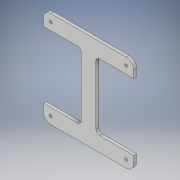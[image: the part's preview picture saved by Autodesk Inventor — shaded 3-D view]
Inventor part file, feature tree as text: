
AUTODESK INVENTOR PART (.ipt)
format: ipt  version: 2019 (Build 230136000, 136)  size: 139,776 bytes
history: native  units: in
note: dims shown in document units (in); Inventor stores cm internally (conversion verified against a paired STEP export)
features: reference x11, other x6, extrude x2, sketch x2
ambient origin geometry x8: Origin, YZ Plane, XZ Plane, XY Plane, X Axis, Y Axis, Z Axis, Center Point
bodies: Solid1 (feature_tree)
feature tree (21):
  extrude  "Extrusion1"  Depth=0.25in
  extrude  "Extrusion2"  Depth=0.25in
  sketch  "Sketch1"  dims[d0=0.1in d1=0.0in d2=0.25in]
  reference  "Reference1"
  reference  "Reference2"
  reference  "Reference3"
  reference  "Reference4"
  reference  "Reference5"
  reference  "Reference6"
  reference  "Reference7"
  reference  "Reference8"
  reference  "Reference9"
  reference  "Reference10"
  reference  "Reference11"
  sketch  "Sketch2"  dims[d3=0.25in d5=0.25in d6=0.25in d7=0.25in d8=0.125in d9=0.1in d10=0.0in]
  other  "<userpath>\Documents\Inventor\Glyptodon Head\Head Assemble.iam"
  other  "Head Assemble.iam"
  other  "Head Workable With Mouth:1"
  other  "<userpath>\Documents\Glyptodon Work\Glyptodon.iam"
  other  "Glyptodon.iam"
  other  "Frame:1"
